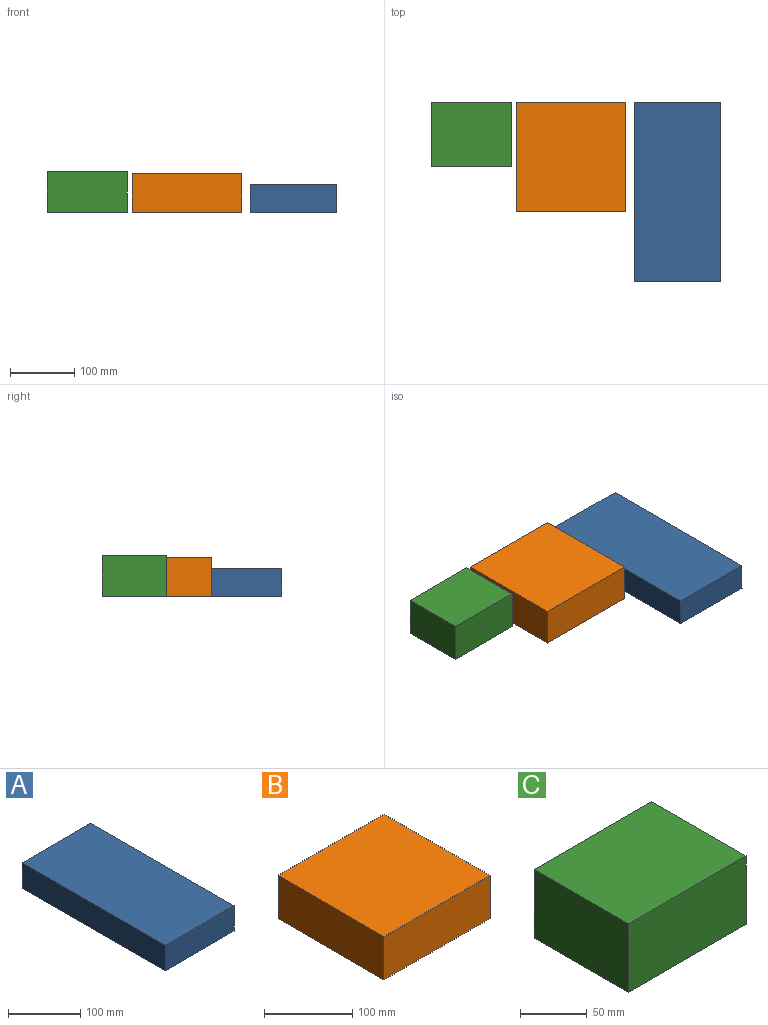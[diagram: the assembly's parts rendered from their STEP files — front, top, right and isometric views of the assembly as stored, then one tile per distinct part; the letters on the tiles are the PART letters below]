
ASSEMBLY  parts=3 mates=4
PART A: 6 faces, bbox 135x280x43 mm
  f0: plane 135x43mm, normal (0,1,0), area 5805mm2, adj f1,f3,f4,f5
  f1: plane 280x43mm, normal (-1,0,0), area 12040mm2, adj f0,f2,f4,f5
  f2: plane 135x43mm, normal (0,-1,0), area 5805mm2, adj f1,f3,f4,f5
  f3: plane 280x43mm, normal (1,0,0), area 12040mm2, adj f0,f2,f4,f5
  f4: plane 280x135mm, normal (0,0,1), area 37800mm2, adj f0,f1,f2,f3
  f5: plane 280x135mm, normal (0,0,-1), area 37800mm2, adj f0,f1,f2,f3
PART B: 6 faces, bbox 170.2x170.2x60 mm
  f0: plane 170.18x60mm, normal (0,1,0), area 10210.8mm2, adj f1,f3,f4,f5
  f1: plane 170.18x60mm, normal (-1,0,0), area 10210.8mm2, adj f0,f2,f4,f5
  f2: plane 170.18x60mm, normal (0,-1,0), area 10210.8mm2, adj f1,f3,f4,f5
  f3: plane 170.18x60mm, normal (1,0,0), area 10210.8mm2, adj f0,f2,f4,f5
  f4: plane 170.18x170.18mm, normal (0,0,1), area 28961.2mm2, adj f0,f1,f2,f3
  f5: plane 170.18x170.18mm, normal (0,0,-1), area 28961.2mm2, adj f0,f1,f2,f3
PART C: 6 faces, bbox 125x100x63 mm
  f0: plane 125x63mm, normal (0,1,0), area 7875mm2, adj f1,f3,f4,f5
  f1: plane 100x63mm, normal (-1,0,0), area 6300mm2, adj f0,f2,f4,f5
  f2: plane 125x63mm, normal (0,-1,0), area 7875mm2, adj f1,f3,f4,f5
  f3: plane 100x63mm, normal (1,0,0), area 6300mm2, adj f0,f2,f4,f5
  f4: plane 125x100mm, normal (0,0,1), area 12500mm2, adj f0,f1,f2,f3
  f5: plane 125x100mm, normal (0,0,-1), area 12500mm2, adj f0,f1,f2,f3
PLACE A rot(axis=(-0.29,-0.9,0.34),0deg) t=(-247.26,-147.43,-257.2)mm
PLACE B rot(axis=(-0.29,-0.9,0.34),0deg) t=(-578.37,-147.43,-257.2)mm
PLACE C rot(axis=(-0.29,-0.9,0.34),0deg) t=(-424.3,-127.89,-257.2)mm
MATE planar C.f0 <-> A.f0  axis (0,1,0) through (-569.54,132.57,-225.7)mm
MATE planar B.f5 <-> C.f5  axis (0,0,-1) through (-413.63,47.48,-257.2)mm
MATE planar A.f5 <-> C.f5  axis (0,0,-1) through (-247.26,-7.43,-257.2)mm
MATE planar B.f0 <-> A.f0  axis (0,1,0) through (-413.63,132.57,-227.2)mm
